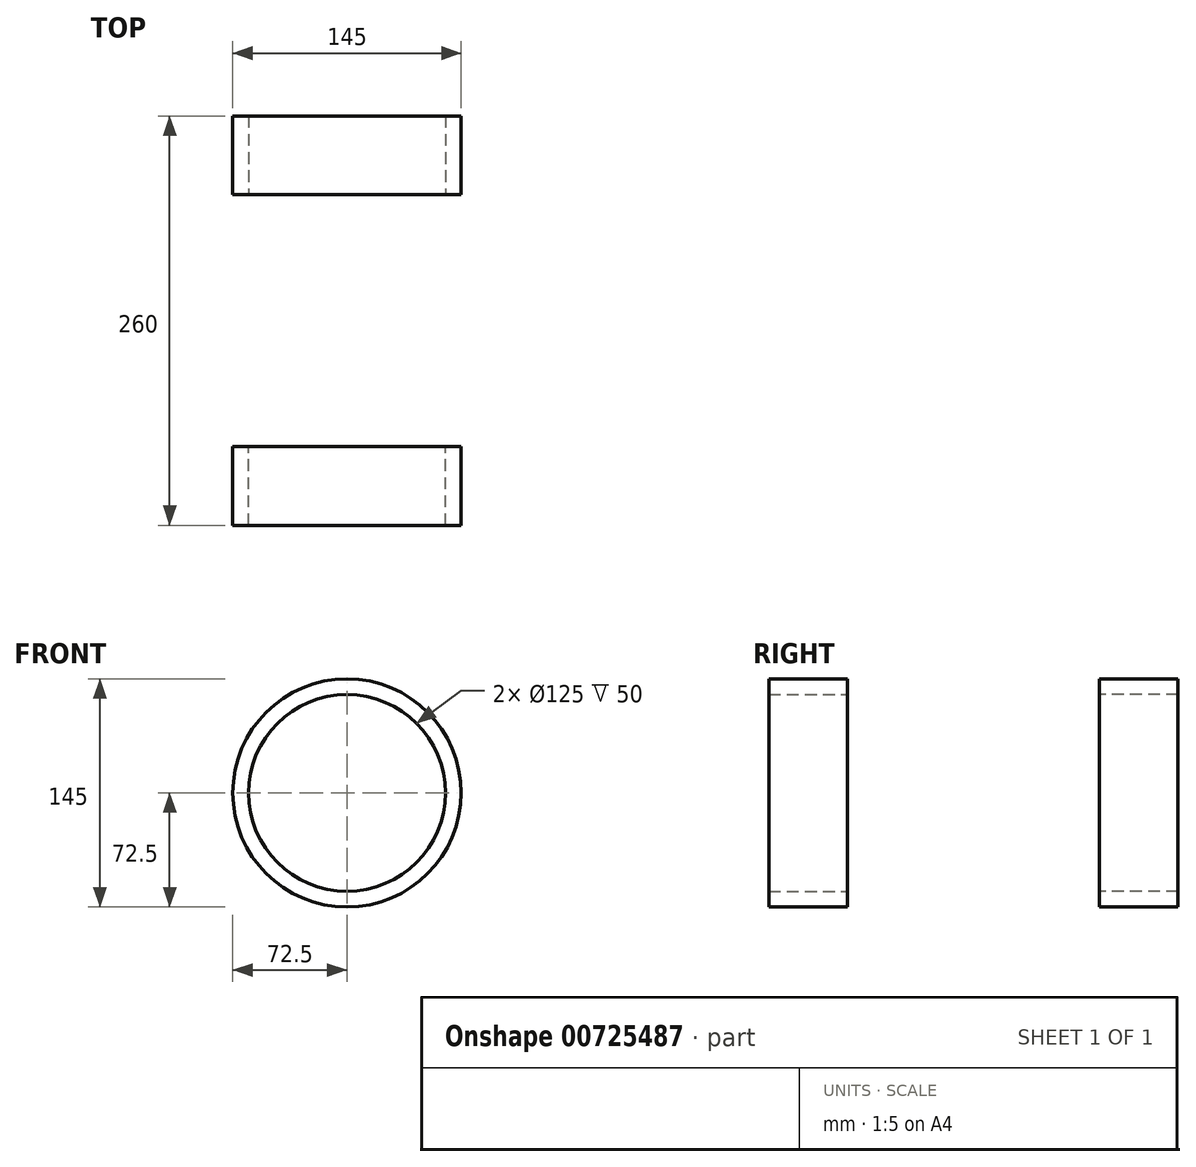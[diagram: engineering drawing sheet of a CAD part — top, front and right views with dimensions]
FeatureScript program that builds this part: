
annotation { "Feature Type Name" : "Feature", "Feature Type Description" : "" }
export const myFeature = defineFeature(function(context is Context, id is Id, definition is map)
    precondition{}
    {
        {
            var Q0;
            Q0=qCreatedBy(makeId("Front.planeOp"),FACE);
            var sketch = newSketch(context, id + "F0", { "sketchPlane" : qUnion([Q0])});
            skCircle(sketch, "E0", {"center": v(0, 0) * mm, "radius": 62.5 * mm});
            skCircle(sketch, "E1.0", {"center": v(0, 0) * mm, "radius": 72.5 * mm});
            skSolve(sketch);
        }
        {
            var Q0;
            Q0=makeQuery(id+"F0.imprint","IMPRINT",FACE,{"disambiguationData":[TD([[makeQuery(id+"F0.imprint","IMPRINT",EDGE,{"derivedFrom":sQuery(id+"F0.wireOp",EDGE,"E0")}),-1.0]])]});
            extrude(context, id + "F1", {"entities" : qUnion([Q0]), "depth" : 50 * mm, "offsetDistance" : 25 * mm});
        }
        {
            var Q0;
            Q0=qCreatedBy(makeId("Front.planeOp"),FACE);
            cPlane(context, id + "F2", {"entities" : qUnion([Q0]), "cplaneType" : CPlaneType.OFFSET, "offset" : 80 * mm, "oppositeDirection" : true, "width" : 150 * mm, "height" : 150 * mm});
        }
        {
            var Q0;
            Q0=makeQuery(id+"F1.opExtrude","SWEPT_BODY",BODY,{"disambiguationData":[OSD([sQuery(id+"F0.wireOp",EDGE,"E0"),sQuery(id+"F0.wireOp",EDGE,"E1.0")])]});
            var Q1;
            Q1=qCreatedBy(id+"F2.planeOp",FACE);
            mirror(context, id + "F3", {"entities" : qUnion([Q0]), "mirrorPlane" : qUnion([Q1])});
        }
    });
